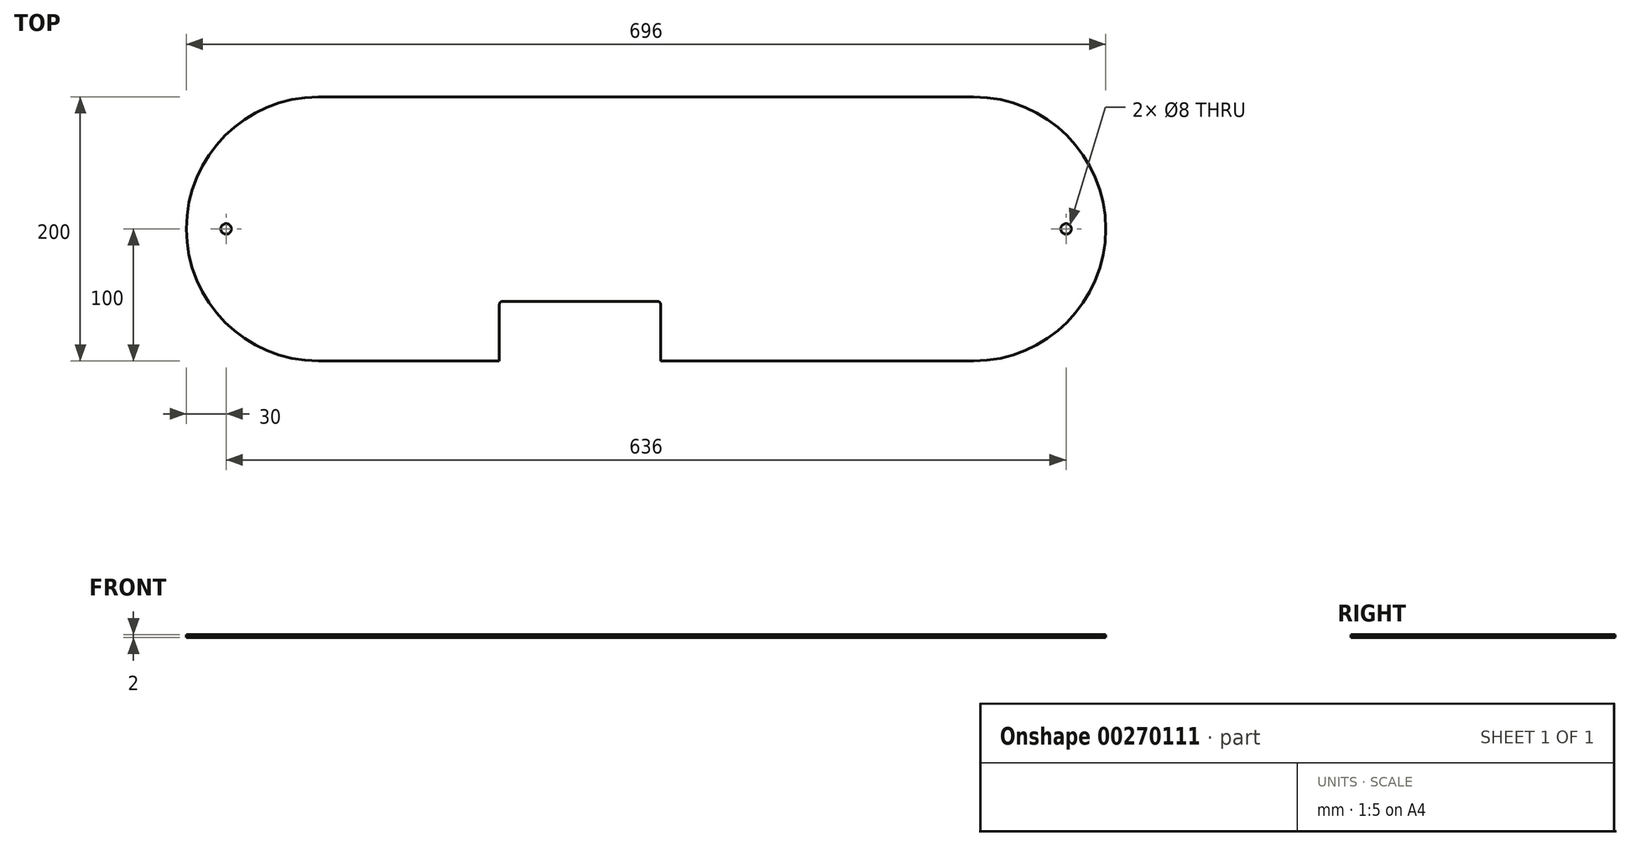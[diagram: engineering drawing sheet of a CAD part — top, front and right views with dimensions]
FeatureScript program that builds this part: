
annotation { "Feature Type Name" : "Feature", "Feature Type Description" : "" }
export const myFeature = defineFeature(function(context is Context, id is Id, definition is map)
    precondition{}
    {
        {
            var Q0;
            Q0=qCreatedBy(makeId("Top.planeOp"),FACE);
            var sketch = newSketch(context, id + "F0", { "sketchPlane" : qUnion([Q0])});
            skLineSegment(sketch, "E0.bottom", {"start": v(248, -100) * mm, "end": v(-248, -100) * mm});
            skLineSegment(sketch, "E0.top", {"start": v(248, 100) * mm, "end": v(-248, 100) * mm});
            skPoint(sketch, "E0.middle", {"position": v(0, 0) * mm});
            skArc(sketch, "E1", {"start": v(248, -100) * mm, "mid": v(348, 0) * mm, "end": v(248, 100) * mm});
            skArc(sketch, "E2", {"start": v(-248, 100) * mm, "mid": v(-348, 0) * mm, "end": v(-248, -100) * mm});
            skPoint(sketch, "E3", {"position": v(0, 100) * mm});
            skSolve(sketch);
        }
        {
            var Q0;
            Q0=makeQuery(id+"F0.imprint","IMPRINT",FACE,{"disambiguationData":[TD([[makeQuery(id+"F0.imprint","IMPRINT",EDGE,{"derivedFrom":sQuery(id+"F0.wireOp",EDGE,"E0.bottom")}),-1.0]])]});
            extrude(context, id + "F1", {"entities" : qUnion([Q0]), "depth" : 2 * mm});
        }
        {
            var Q0;
            Q0=makeQuery(id+"F1.opExtrude","CAP_FACE",FACE,{"disambiguationData":[OSD([sQuery(id+"F0.wireOp",EDGE,"E0.bottom"),sQuery(id+"F0.wireOp",EDGE,"E0.top"),sQuery(id+"F0.wireOp",EDGE,"E1"),sQuery(id+"F0.wireOp",EDGE,"E2")])],"isStart":false});
            var sketch = newSketch(context, id + "F2", { "sketchPlane" : qUnion([Q0])});
            skCircle(sketch, "E4", {"center": v(-318, 0) * mm, "radius": 4 * mm});
            skCircle(sketch, "E5", {"center": v(318, 0) * mm, "radius": 4 * mm});
            skLineSegment(sketch, "E6.bottom", {"start": v(-111, -55) * mm, "end": v(11, -55) * mm});
            skLineSegment(sketch, "E6.top", {"start": v(-111, -100) * mm, "end": v(11, -100) * mm});
            skLineSegment(sketch, "E6.left", {"start": v(-111, -55) * mm, "end": v(-111, -100) * mm});
            skLineSegment(sketch, "E6.right", {"start": v(11, -55) * mm, "end": v(11, -100) * mm});
            skSolve(sketch);
        }
        {
            var Q0;
            Q0=makeQuery(id+"F2.imprint","IMPRINT",FACE,{"disambiguationData":[TD([[makeQuery(id+"F2.imprint","IMPRINT",EDGE,{"derivedFrom":sQuery(id+"F2.wireOp",EDGE,"E5")}),1.0]])]});
            var Q1;
            Q1=makeQuery(id+"F2.imprint","IMPRINT",FACE,{"disambiguationData":[TD([[makeQuery(id+"F2.imprint","IMPRINT",EDGE,{"derivedFrom":sQuery(id+"F2.wireOp",EDGE,"E4")}),1.0]])]});
            var Q2;
            Q2=makeQuery(id+"F2.imprint","IMPRINT",FACE,{"disambiguationData":[TD([[makeQuery(id+"F2.imprint","IMPRINT",EDGE,{"derivedFrom":sQuery(id+"F2.wireOp",EDGE,"E6.bottom")}),-1.0]])]});
            extrude(context, id + "F3", {"entities" : qUnion([Q0, Q1, Q2]), "operationType" : NewBodyOperationType.REMOVE, "endBound" : BoundingType.UP_TO_NEXT, "oppositeDirection" : true, "depth" : 25 * mm});
        }
        {
            var Q0;
            Q0=makeQuery(id+"F3.boolean.opBoolean","COPY",EDGE,{"derivedFrom":makeQuery(id+"F3.opExtrude","SWEPT_EDGE",EDGE,{"disambiguationData":[OSD([sQuery(id+"F2.wireOp",EDGE,"E6.bottom"),sQuery(id+"F2.wireOp",EDGE,"E6.right")])]})});
            var Q1;
            Q1=makeQuery(id+"F3.boolean.opBoolean","COPY",EDGE,{"derivedFrom":makeQuery(id+"F3.opExtrude","SWEPT_EDGE",EDGE,{"disambiguationData":[OSD([sQuery(id+"F2.wireOp",EDGE,"E6.bottom"),sQuery(id+"F2.wireOp",EDGE,"E6.left")])]})});
            fillet(context, id + "F4", {"entities" : qUnion([Q0, Q1]), "radius" : 2 * mm, "tangentPropagation" : true, "allowEdgeOverflow" : false});
        }
    });
